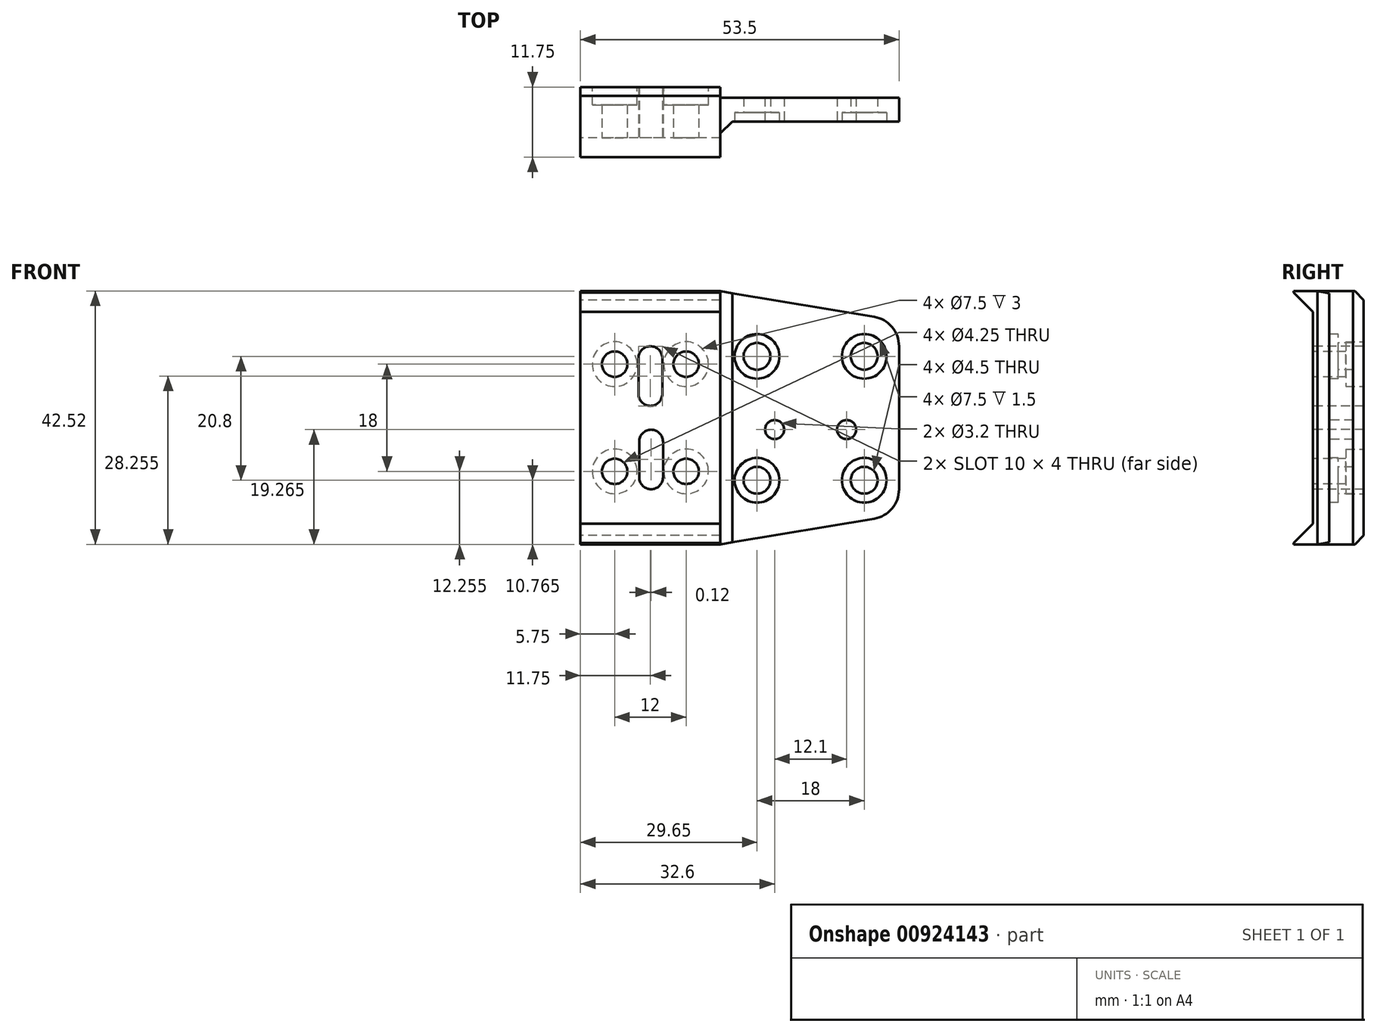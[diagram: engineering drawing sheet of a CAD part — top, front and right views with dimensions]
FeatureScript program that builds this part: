
annotation { "Feature Type Name" : "Feature", "Feature Type Description" : "" }
export const myFeature = defineFeature(function(context is Context, id is Id, definition is map)
    precondition{}
    {
        {
            var Q0;
            Q0=qCreatedBy(makeId("Front.planeOp"),FACE);
            var sketch = newSketch(context, id + "F0", { "sketchPlane" : qUnion([Q0])});
            skLineSegment(sketch, "E0.bottom", {"start": v(11.75, -21.26) * mm, "end": v(-11.75, -21.26) * mm});
            skLineSegment(sketch, "E0.top", {"start": v(11.75, 21.25) * mm, "end": v(-11.75, 21.25) * mm});
            skLineSegment(sketch, "E0.left", {"start": v(11.75, -21.25) * mm, "end": v(11.75, 21.26) * mm});
            skLineSegment(sketch, "E0.right", {"start": v(-11.75, -21.26) * mm, "end": v(-11.75, 21.25) * mm});
            skPoint(sketch, "E0.middle", {"position": v(0, 0) * mm});
            skSolve(sketch);
        }
        {
            var Q0;
            Q0=qSketchRegion(id+"F0",true);
            extrude(context, id + "F1", {"entities" : qUnion([Q0]), "depth" : 9 * mm});
        }
        {
            var Q0;
            Q0=makeQuery(id+"F1.opExtrude","CAP_FACE",FACE,{"disambiguationData":[OSD([sQuery(id+"F0.wireOp",EDGE,"E0.bottom"),sQuery(id+"F0.wireOp",EDGE,"E0.top"),sQuery(id+"F0.wireOp",EDGE,"E0.left"),sQuery(id+"F0.wireOp",EDGE,"E0.right")])],"isStart":false});
            var sketch = newSketch(context, id + "F2", { "sketchPlane" : qUnion([Q0])});
            skCircle(sketch, "E1", {"center": v(-6, 9) * mm, "radius": 2.12 * mm});
            skCircle(sketch, "E2.1.0.0", {"center": v(6, 9) * mm, "radius": 2.12 * mm});
            skLineSegment(sketch, "E2.direction1", {"start": v(-6, 9) * mm, "end": v(6, 9) * mm, "construction": true});
            skCircle(sketch, "E3.1.0.0", {"center": v(-6, -9) * mm, "radius": 2.12 * mm});
            skCircle(sketch, "E3.1.0.1", {"center": v(6, -9) * mm, "radius": 2.12 * mm});
            skLineSegment(sketch, "E3.direction1", {"start": v(-6, -9) * mm, "end": v(-6, 9) * mm, "construction": true});
            skArc(sketch, "E4", {"start": v(2, 10) * mm, "mid": v(0, 12) * mm, "end": v(-2, 10) * mm});
            skLineSegment(sketch, "E5.left", {"start": v(2, 10) * mm, "end": v(2, 4) * mm});
            skLineSegment(sketch, "E5.right", {"start": v(-2, 10) * mm, "end": v(-2, 4) * mm});
            skArc(sketch, "E6", {"start": v(-2, 4) * mm, "mid": v(0, 2) * mm, "end": v(2, 4) * mm});
            skArc(sketch, "E7.1.0.0", {"start": v(2.12, -4) * mm, "mid": v(0.12, -2) * mm, "end": v(-1.88, -4) * mm});
            skLineSegment(sketch, "E7.1.0.1", {"start": v(2.12, -4) * mm, "end": v(2.12, -10) * mm});
            skArc(sketch, "E7.1.0.2", {"start": v(-1.88, -10) * mm, "mid": v(0.12, -12) * mm, "end": v(2.12, -10) * mm});
            skLineSegment(sketch, "E7.1.0.3", {"start": v(-1.88, -4) * mm, "end": v(-1.88, -10) * mm});
            skLineSegment(sketch, "E7.direction1", {"start": v(-2, 10) * mm, "end": v(-1.88, -4) * mm, "construction": true});
            skSolve(sketch);
        }
        {
            var Q0;
            Q0=makeQuery(id+"F2.imprint","IMPRINT",FACE,{"disambiguationData":[TD([[makeQuery(id+"F2.imprint","IMPRINT",EDGE,{"derivedFrom":sQuery(id+"F2.wireOp",EDGE,"E1")}),1.0]])]});
            var Q1;
            Q1=makeQuery(id+"F2.imprint","IMPRINT",FACE,{"disambiguationData":[TD([[makeQuery(id+"F2.imprint","IMPRINT",EDGE,{"derivedFrom":sQuery(id+"F2.wireOp",EDGE,"E4")}),1.0]])]});
            var Q2;
            Q2=makeQuery(id+"F2.imprint","IMPRINT",FACE,{"disambiguationData":[TD([[makeQuery(id+"F2.imprint","IMPRINT",EDGE,{"derivedFrom":sQuery(id+"F2.wireOp",EDGE,"E2.1.0.0")}),1.0]])]});
            var Q3;
            Q3=makeQuery(id+"F2.imprint","IMPRINT",FACE,{"disambiguationData":[TD([[makeQuery(id+"F2.imprint","IMPRINT",EDGE,{"derivedFrom":sQuery(id+"F2.wireOp",EDGE,"E3.1.0.1")}),1.0]])]});
            var Q4;
            Q4=makeQuery(id+"F2.imprint","IMPRINT",FACE,{"disambiguationData":[TD([[makeQuery(id+"F2.imprint","IMPRINT",EDGE,{"derivedFrom":sQuery(id+"F2.wireOp",EDGE,"E7.1.0.0")}),1.0]])]});
            var Q5;
            Q5=makeQuery(id+"F2.imprint","IMPRINT",FACE,{"disambiguationData":[TD([[makeQuery(id+"F2.imprint","IMPRINT",EDGE,{"derivedFrom":sQuery(id+"F2.wireOp",EDGE,"E3.1.0.0")}),1.0]])]});
            extrude(context, id + "F3", {"entities" : qUnion([Q0, Q1, Q2, Q3, Q4, Q5]), "operationType" : NewBodyOperationType.REMOVE, "endBound" : BoundingType.THROUGH_ALL, "oppositeDirection" : true, "depth" : 25 * mm});
        }
        {
            var Q0;
            Q0=makeQuery(id+"F1.opExtrude","SWEPT_FACE",FACE,{"disambiguationData":[OSD([sQuery(id+"F0.wireOp",EDGE,"E0.right")])]});
            var sketch = newSketch(context, id + "F4", { "sketchPlane" : qUnion([Q0])});
            skLineSegment(sketch, "E8", {"start": v(9, 21.25) * mm, "end": v(12.25, 21.25) * mm});
            skLineSegment(sketch, "E9", {"start": v(12.25, 21.25) * mm, "end": v(12.25, 21) * mm});
            skLineSegment(sketch, "E10", {"start": v(12.25, 21) * mm, "end": v(9, 17.75) * mm});
            skLineSegment(sketch, "E11", {"start": v(9, 17.75) * mm, "end": v(9, 21.25) * mm});
            skLineSegment(sketch, "E12", {"start": v(0, 0) * mm, "end": v(9, 0) * mm});
            skLineSegment(sketch, "E13.MirrorCS", {"start": v(9, -21.26) * mm, "end": v(12.25, -21.26) * mm});
            skLineSegment(sketch, "E14.MirrorCS", {"start": v(9, -17.76) * mm, "end": v(9, -21.26) * mm});
            skLineSegment(sketch, "E15.MirrorCS", {"start": v(12.25, -21) * mm, "end": v(9, -17.76) * mm});
            skLineSegment(sketch, "E16.MirrorCS", {"start": v(12.25, -21.26) * mm, "end": v(12.25, -21) * mm});
            skSolve(sketch);
        }
        {
            var Q0;
            Q0=makeQuery(id+"F4.imprint","IMPRINT",FACE,{"disambiguationData":[TD([[makeQuery(id+"F4.imprint","IMPRINT",EDGE,{"derivedFrom":sQuery(id+"F4.wireOp",EDGE,"E8")}),-1.0]])]});
            var Q1;
            Q1=makeQuery(id+"F4.imprint","IMPRINT",FACE,{"disambiguationData":[TD([[makeQuery(id+"F4.imprint","IMPRINT",EDGE,{"derivedFrom":sQuery(id+"F4.wireOp",EDGE,"E13.MirrorCS")}),1.0]])]});
            extrude(context, id + "F5", {"entities" : qUnion([Q0, Q1]), "operationType" : NewBodyOperationType.ADD, "oppositeDirection" : true, "depth" : 23.5 * mm});
        }
        {
            var Q0;
            Q0=makeQuery(id+"F1.opExtrude","CAP_EDGE",EDGE,{"disambiguationData":[OSD([sQuery(id+"F0.wireOp",EDGE,"E0.top")])],"isStart":true});
            var Q1;
            Q1=makeQuery(id+"F1.opExtrude","CAP_EDGE",EDGE,{"disambiguationData":[OSD([sQuery(id+"F0.wireOp",EDGE,"E0.bottom")])],"isStart":true});
            chamfer(context, id + "F6", {"entities" : qUnion([Q0, Q1]), "width" : 2 * mm, "tangentPropagation" : true});
        }
        {
            var Q0;
            Q0=makeQuery(id+"F5.boolean.opBoolean","MERGE",FACE,{"derivedFrom":[makeQuery(id+"F1.opExtrude","SWEPT_FACE",FACE,{"disambiguationData":[OSD([sQuery(id+"F0.wireOp",EDGE,"E0.left")])]}),makeQuery(id+"F5.opExtrude","CAP_FACE",FACE,{"disambiguationData":[OSD([sQuery(id+"F4.wireOp",EDGE,"E8"),sQuery(id+"F4.wireOp",EDGE,"E9"),sQuery(id+"F4.wireOp",EDGE,"E10"),sQuery(id+"F4.wireOp",EDGE,"E11")])],"isStart":false}),makeQuery(id+"F5.opExtrude","CAP_FACE",FACE,{"disambiguationData":[OSD([sQuery(id+"F4.wireOp",EDGE,"E13.MirrorCS"),sQuery(id+"F4.wireOp",EDGE,"E14.MirrorCS"),sQuery(id+"F4.wireOp",EDGE,"E15.MirrorCS"),sQuery(id+"F4.wireOp",EDGE,"E16.MirrorCS")])],"isStart":false})]});
            var sketch = newSketch(context, id + "F7", { "sketchPlane" : qUnion([Q0])});
            skLineSegment(sketch, "E17.bottom", {"start": v(-2.27, 21.25) * mm, "end": v(-6.27, 21.25) * mm});
            skLineSegment(sketch, "E17.top", {"start": v(-2.27, -21.25) * mm, "end": v(-6.27, -21.25) * mm});
            skLineSegment(sketch, "E17.left", {"start": v(-2.27, 21.25) * mm, "end": v(-2.27, -21.25) * mm});
            skLineSegment(sketch, "E17.right", {"start": v(-6.27, 21.25) * mm, "end": v(-6.27, -21.25) * mm});
            skSolve(sketch);
        }
        {
            var Q0;
            Q0=makeQuery(id+"F7.imprint","IMPRINT",FACE,{"disambiguationData":[TD([[makeQuery(id+"F7.imprint","IMPRINT",EDGE,{"derivedFrom":sQuery(id+"F7.wireOp",EDGE,"E17.bottom")}),1.0]])]});
            extrude(context, id + "F8", {"entities" : qUnion([Q0]), "operationType" : NewBodyOperationType.ADD, "depth" : 30 * mm});
        }
        {
            var Q0;
            Q0=makeQuery(id+"F8.opExtrude","SWEPT_FACE",FACE,{"disambiguationData":[OSD([sQuery(id+"F7.wireOp",EDGE,"E17.right")])]});
            var sketch = newSketch(context, id + "F9", { "sketchPlane" : qUnion([Q0])});
            skCircle(sketch, "E18", {"center": v(17.9, -10.5) * mm, "radius": 2.25 * mm});
            skCircle(sketch, "E19.0.1.0", {"center": v(17.9, 10.3) * mm, "radius": 2.25 * mm});
            skCircle(sketch, "E19.1.0.0", {"center": v(35.9, -10.5) * mm, "radius": 2.25 * mm});
            skCircle(sketch, "E19.1.1.0", {"center": v(35.9, 10.3) * mm, "radius": 2.25 * mm});
            skLineSegment(sketch, "E19.direction1", {"start": v(17.9, -10.5) * mm, "end": v(35.9, -10.5) * mm, "construction": true});
            skLineSegment(sketch, "E19.direction2", {"start": v(17.9, -10.5) * mm, "end": v(17.9, 10.3) * mm, "construction": true});
            skCircle(sketch, "E20", {"center": v(32.95, -2) * mm, "radius": 1.6 * mm});
            skCircle(sketch, "E21.1.0.0", {"center": v(20.85, -2) * mm, "radius": 1.6 * mm});
            skLineSegment(sketch, "E21.direction1", {"start": v(32.95, -2) * mm, "end": v(20.85, -2) * mm, "construction": true});
            skSolve(sketch);
        }
        {
            var Q0;
            Q0=makeQuery(id+"F9.imprint","IMPRINT",FACE,{"disambiguationData":[TD([[makeQuery(id+"F9.imprint","IMPRINT",EDGE,{"derivedFrom":sQuery(id+"F9.wireOp",EDGE,"E19.0.1.0")}),1.0]])]});
            var Q1;
            Q1=makeQuery(id+"F9.imprint","IMPRINT",FACE,{"disambiguationData":[TD([[makeQuery(id+"F9.imprint","IMPRINT",EDGE,{"derivedFrom":sQuery(id+"F9.wireOp",EDGE,"E19.1.1.0")}),1.0]])]});
            var Q2;
            Q2=makeQuery(id+"F9.imprint","IMPRINT",FACE,{"disambiguationData":[TD([[makeQuery(id+"F9.imprint","IMPRINT",EDGE,{"derivedFrom":sQuery(id+"F9.wireOp",EDGE,"E21.1.0.0")}),1.0]])]});
            var Q3;
            Q3=makeQuery(id+"F9.imprint","IMPRINT",FACE,{"disambiguationData":[TD([[makeQuery(id+"F9.imprint","IMPRINT",EDGE,{"derivedFrom":sQuery(id+"F9.wireOp",EDGE,"E20")}),1.0]])]});
            var Q4;
            Q4=makeQuery(id+"F9.imprint","IMPRINT",FACE,{"disambiguationData":[TD([[makeQuery(id+"F9.imprint","IMPRINT",EDGE,{"derivedFrom":sQuery(id+"F9.wireOp",EDGE,"E18")}),1.0]])]});
            var Q5;
            Q5=makeQuery(id+"F9.imprint","IMPRINT",FACE,{"disambiguationData":[TD([[makeQuery(id+"F9.imprint","IMPRINT",EDGE,{"derivedFrom":sQuery(id+"F9.wireOp",EDGE,"E19.1.0.0")}),1.0]])]});
            extrude(context, id + "F10", {"entities" : qUnion([Q0, Q1, Q2, Q3, Q4, Q5]), "operationType" : NewBodyOperationType.REMOVE, "endBound" : BoundingType.THROUGH_ALL, "oppositeDirection" : true, "depth" : 25 * mm});
        }
        {
            var Q0;
            Q0=makeQuery(id+"F8.opExtrude","SWEPT_FACE",FACE,{"disambiguationData":[OSD([sQuery(id+"F7.wireOp",EDGE,"E17.right")])]});
            var sketch = newSketch(context, id + "F11", { "sketchPlane" : qUnion([Q0])});
            skCircle(sketch, "E22", {"center": v(17.9, 10.3) * mm, "radius": 3.75 * mm});
            skCircle(sketch, "E23", {"center": v(35.9, 10.3) * mm, "radius": 3.75 * mm});
            skCircle(sketch, "E24", {"center": v(35.9, -10.5) * mm, "radius": 3.75 * mm});
            skCircle(sketch, "E25", {"center": v(17.9, -10.5) * mm, "radius": 3.75 * mm});
            skSolve(sketch);
        }
        {
            var Q0;
            Q0=makeQuery(id+"F11.imprint","IMPRINT",FACE,{"disambiguationData":[TD([[makeQuery(id+"F11.imprint","IMPRINT",EDGE,{"derivedFrom":sQuery(id+"F11.wireOp",EDGE,"E22")}),1.0]])]});
            var Q1;
            Q1=makeQuery(id+"F11.imprint","IMPRINT",FACE,{"disambiguationData":[TD([[makeQuery(id+"F11.imprint","IMPRINT",EDGE,{"derivedFrom":sQuery(id+"F11.wireOp",EDGE,"E23")}),1.0]])]});
            var Q2;
            Q2=makeQuery(id+"F11.imprint","IMPRINT",FACE,{"disambiguationData":[TD([[makeQuery(id+"F11.imprint","IMPRINT",EDGE,{"derivedFrom":sQuery(id+"F11.wireOp",EDGE,"E24")}),1.0]])]});
            var Q3;
            Q3=makeQuery(id+"F11.imprint","IMPRINT",FACE,{"disambiguationData":[TD([[makeQuery(id+"F11.imprint","IMPRINT",EDGE,{"derivedFrom":sQuery(id+"F11.wireOp",EDGE,"E25")}),1.0]])]});
            extrude(context, id + "F12", {"entities" : qUnion([Q0, Q1, Q2, Q3]), "operationType" : NewBodyOperationType.REMOVE, "oppositeDirection" : true, "depth" : 1.5 * mm});
        }
        {
            var Q0;
            Q0=makeQuery(id+"F8.opExtrude","CAP_EDGE",EDGE,{"disambiguationData":[OSD([sQuery(id+"F7.wireOp",EDGE,"E17.bottom")])],"isStart":false});
            var Q1;
            Q1=makeQuery(id+"F8.opExtrude","CAP_EDGE",EDGE,{"disambiguationData":[OSD([sQuery(id+"F7.wireOp",EDGE,"E17.top")])],"isStart":false});
            chamfer(context, id + "F13", {"entities" : qUnion([Q0, Q1]), "chamferType" : ChamferType.TWO_OFFSETS, "width1" : 5 * mm, "oppositeDirection" : false, "width2" : 30 * mm, "tangentPropagation" : true});
        }
        {
            var Q0;
            {var subQ0=sQuery(id+"F7.wireOp",EDGE,"E17.bottom");Q0=makeQuery(id+"F13.opChamfer","BLEND_EDGE",EDGE,{"blendedFrom":[makeQuery(id+"F8.opExtrude","CAP_EDGE",EDGE,{"disambiguationData":[OSD([subQ0])],"isStart":false}),makeQuery(id+"F8.opExtrude","CAP_FACE",FACE,{"disambiguationData":[OSD([subQ0,sQuery(id+"F7.wireOp",EDGE,"E17.top"),sQuery(id+"F7.wireOp",EDGE,"E17.left"),sQuery(id+"F7.wireOp",EDGE,"E17.right")])],"isStart":false})],"blendedInto":[makeQuery(id+"F8.opExtrude","CAP_FACE",FACE,{"disambiguationData":[OSD([subQ0,sQuery(id+"F7.wireOp",EDGE,"E17.top"),sQuery(id+"F7.wireOp",EDGE,"E17.left"),sQuery(id+"F7.wireOp",EDGE,"E17.right")])],"isStart":false})]});}
            var Q1;
            {var subQ0=sQuery(id+"F7.wireOp",EDGE,"E17.top");Q1=makeQuery(id+"F13.opChamfer","BLEND_EDGE",EDGE,{"blendedFrom":[makeQuery(id+"F8.opExtrude","CAP_EDGE",EDGE,{"disambiguationData":[OSD([subQ0])],"isStart":false}),makeQuery(id+"F8.opExtrude","CAP_FACE",FACE,{"disambiguationData":[OSD([sQuery(id+"F7.wireOp",EDGE,"E17.bottom"),subQ0,sQuery(id+"F7.wireOp",EDGE,"E17.left"),sQuery(id+"F7.wireOp",EDGE,"E17.right")])],"isStart":false})],"blendedInto":[makeQuery(id+"F8.opExtrude","CAP_FACE",FACE,{"disambiguationData":[OSD([sQuery(id+"F7.wireOp",EDGE,"E17.bottom"),subQ0,sQuery(id+"F7.wireOp",EDGE,"E17.left"),sQuery(id+"F7.wireOp",EDGE,"E17.right")])],"isStart":false})]});}
            fillet(context, id + "F14", {"entities" : qUnion([Q0, Q1]), "radius" : 5 * mm, "tangentPropagation" : true, "allowEdgeOverflow" : false});
        }
        {
            var Q0;
            Q0=makeQuery(id+"F8.opExtrude","CAP_EDGE",EDGE,{"disambiguationData":[OSD([sQuery(id+"F7.wireOp",EDGE,"E17.right")])],"isStart":true});
            chamfer(context, id + "F15", {"entities" : qUnion([Q0]), "width" : 2 * mm, "tangentPropagation" : true});
        }
        {
            var Q0;
            Q0=makeQuery(id+"F1.opExtrude","CAP_FACE",FACE,{"disambiguationData":[OSD([sQuery(id+"F0.wireOp",EDGE,"E0.bottom"),sQuery(id+"F0.wireOp",EDGE,"E0.top"),sQuery(id+"F0.wireOp",EDGE,"E0.left"),sQuery(id+"F0.wireOp",EDGE,"E0.right")])],"isStart":true});
            var sketch = newSketch(context, id + "F16", { "sketchPlane" : qUnion([Q0])});
            skCircle(sketch, "E26", {"center": v(-6, 9) * mm, "radius": 3.75 * mm});
            skCircle(sketch, "E27", {"center": v(6, 9) * mm, "radius": 3.75 * mm});
            skCircle(sketch, "E28", {"center": v(6, -9) * mm, "radius": 3.75 * mm});
            skCircle(sketch, "E29", {"center": v(-6, -9) * mm, "radius": 3.75 * mm});
            skSolve(sketch);
        }
        {
            var Q0;
            Q0=makeQuery(id+"F16.imprint","IMPRINT",FACE,{"disambiguationData":[TD([[makeQuery(id+"F16.imprint","IMPRINT",EDGE,{"derivedFrom":sQuery(id+"F16.wireOp",EDGE,"E26")}),1.0]])]});
            var Q1;
            Q1=makeQuery(id+"F16.imprint","IMPRINT",FACE,{"disambiguationData":[TD([[makeQuery(id+"F16.imprint","IMPRINT",EDGE,{"derivedFrom":sQuery(id+"F16.wireOp",EDGE,"E27")}),1.0]])]});
            var Q2;
            Q2=makeQuery(id+"F16.imprint","IMPRINT",FACE,{"disambiguationData":[TD([[makeQuery(id+"F16.imprint","IMPRINT",EDGE,{"derivedFrom":sQuery(id+"F16.wireOp",EDGE,"E29")}),1.0]])]});
            var Q3;
            Q3=makeQuery(id+"F16.imprint","IMPRINT",FACE,{"disambiguationData":[TD([[makeQuery(id+"F16.imprint","IMPRINT",EDGE,{"derivedFrom":sQuery(id+"F16.wireOp",EDGE,"E28")}),1.0]])]});
            extrude(context, id + "F17", {"entities" : qUnion([Q0, Q1, Q2, Q3]), "operationType" : NewBodyOperationType.REMOVE, "oppositeDirection" : true, "depth" : 3.5 * mm});
        }
        {
            var Q0;
            Q0=makeQuery(id+"F5.boolean.opBoolean","MERGE",FACE,{"derivedFrom":[makeQuery(id+"F1.opExtrude","SWEPT_FACE",FACE,{"disambiguationData":[OSD([sQuery(id+"F0.wireOp",EDGE,"E0.right")])]}),makeQuery(id+"F5.opExtrude","CAP_FACE",FACE,{"disambiguationData":[OSD([sQuery(id+"F4.wireOp",EDGE,"E8"),sQuery(id+"F4.wireOp",EDGE,"E9"),sQuery(id+"F4.wireOp",EDGE,"E10"),sQuery(id+"F4.wireOp",EDGE,"E11")])],"isStart":true}),makeQuery(id+"F5.opExtrude","CAP_FACE",FACE,{"disambiguationData":[OSD([sQuery(id+"F4.wireOp",EDGE,"E13.MirrorCS"),sQuery(id+"F4.wireOp",EDGE,"E14.MirrorCS"),sQuery(id+"F4.wireOp",EDGE,"E15.MirrorCS"),sQuery(id+"F4.wireOp",EDGE,"E16.MirrorCS")])],"isStart":true})]});
            var sketch = newSketch(context, id + "F18", { "sketchPlane" : qUnion([Q0])});
            skLineSegment(sketch, "E30", {"start": v(0.5, 19.75) * mm, "end": v(0.5, -19.76) * mm});
            skLineSegment(sketch, "E31", {"start": v(0.5, -19.76) * mm, "end": v(0, -19.26) * mm});
            skLineSegment(sketch, "E32", {"start": v(0, -19.26) * mm, "end": v(0, 19.26) * mm});
            skLineSegment(sketch, "E33", {"start": v(0, 19.26) * mm, "end": v(0.5, 19.75) * mm});
            skSolve(sketch);
        }
        {
            var Q0;
            Q0=qSketchRegion(id+"F18",true);
            extrude(context, id + "F19", {"entities" : qUnion([Q0]), "operationType" : NewBodyOperationType.REMOVE, "endBound" : BoundingType.THROUGH_ALL, "oppositeDirection" : true, "depth" : 25 * mm});
        }
    });
